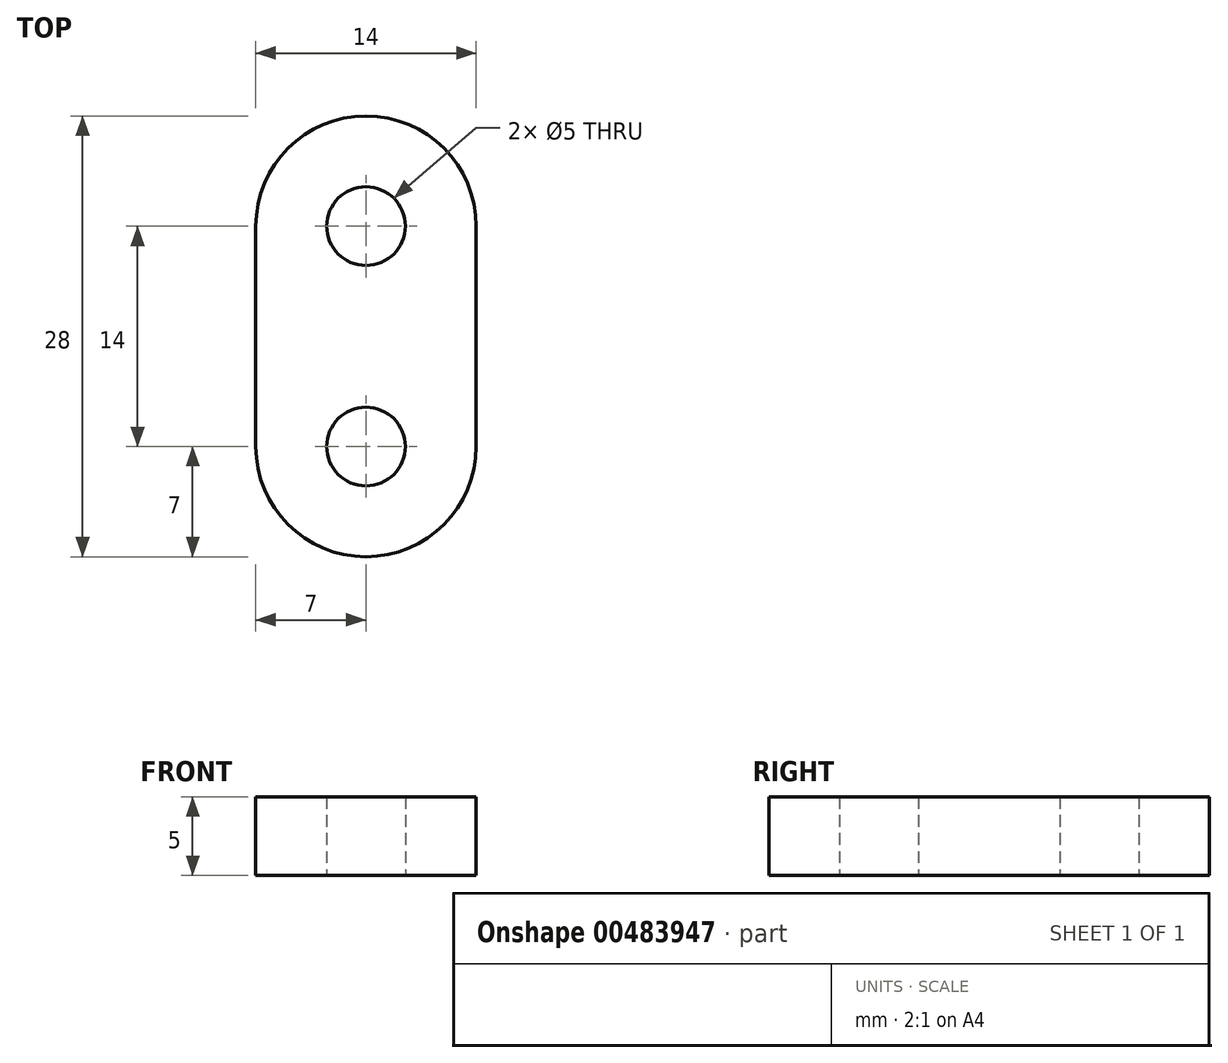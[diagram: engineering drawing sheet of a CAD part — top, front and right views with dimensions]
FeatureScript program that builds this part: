
annotation { "Feature Type Name" : "Feature", "Feature Type Description" : "" }
export const myFeature = defineFeature(function(context is Context, id is Id, definition is map)
    precondition{}
    {
        {
            var Q0;
            Q0=qCreatedBy(makeId("Top.planeOp"),FACE);
            var sketch = newSketch(context, id + "F0", { "sketchPlane" : qUnion([Q0])});
            skCircle(sketch, "E0", {"center": v(0, -7) * mm, "radius": 2.5 * mm});
            skPoint(sketch, "E0.first.point", {"position": v(-1.57, -5.05) * mm});
            skPoint(sketch, "E0.second.point", {"position": v(1.75, -8.78) * mm});
            skPoint(sketch, "E0.third.point", {"position": v(1.85, -5.31) * mm});
            skLineSegment(sketch, "E1", {"start": v(0, 0) * mm, "end": v(0, -4.5) * mm, "construction": true});
            skCircle(sketch, "E2.MirrorC", {"center": v(0, 7) * mm, "radius": 2.5 * mm});
            skArc(sketch, "E3", {"start": v(-7, -7) * mm, "mid": v(0, -14) * mm, "end": v(7, -7) * mm});
            skArc(sketch, "E4", {"start": v(7, 7) * mm, "mid": v(0, 14) * mm, "end": v(-7, 7) * mm});
            skLineSegment(sketch, "E5", {"start": v(-7, 7) * mm, "end": v(-7, -7) * mm});
            skLineSegment(sketch, "E6", {"start": v(7, 7) * mm, "end": v(7, -7.28) * mm});
            skSolve(sketch);
        }
        {
            var Q0;
            Q0=makeQuery(id+"F0.imprint","IMPRINT",FACE,{"disambiguationData":[TD([[makeQuery(id+"F0.imprint","IMPRINT",EDGE,{"derivedFrom":sQuery(id+"F0.wireOp",EDGE,"E0")}),-1.0]])]});
            extrude(context, id + "F1", {"entities" : qUnion([Q0]), "depth" : 5 * mm});
        }
    });
